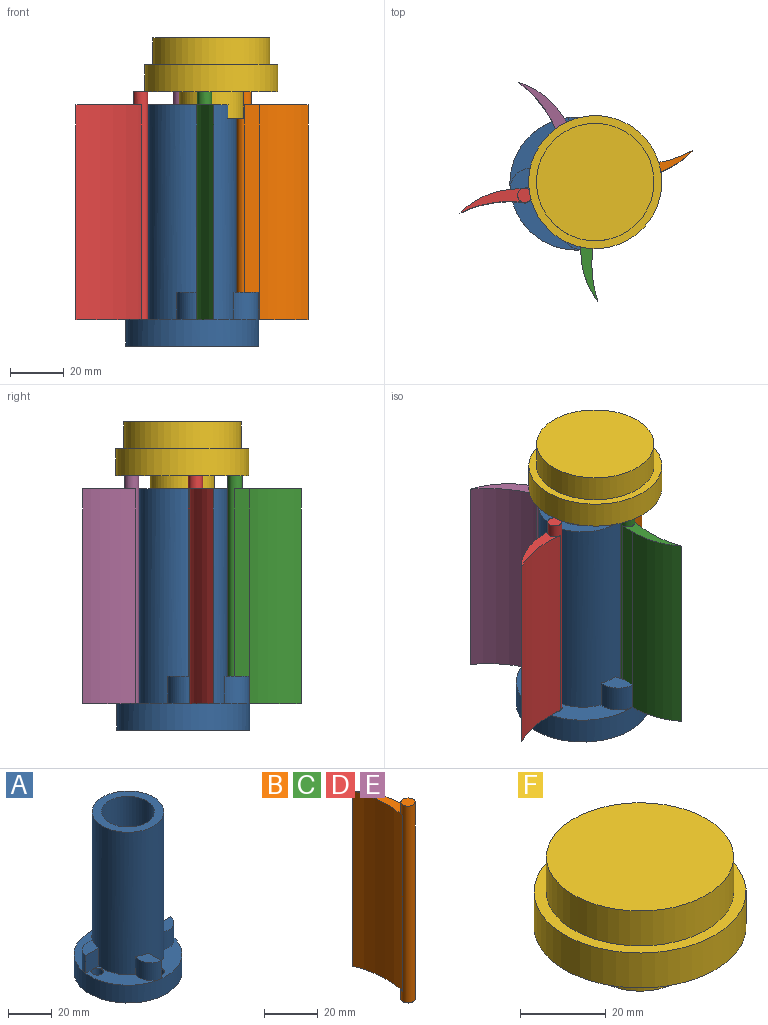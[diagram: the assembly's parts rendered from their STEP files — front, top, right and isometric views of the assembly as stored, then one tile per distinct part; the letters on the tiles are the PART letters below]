
ASSEMBLY  parts=6 mates=5
PART A: 29 faces, bbox 49.6x49.6x90 mm
  f0: plane 27.4x22.05mm, normal (0,0,1), area 194.7mm2, adj f2,f6,f15,f17,f26
  f1: plane 27.4x22.05mm, normal (0,0,1), area 194.7mm2, adj f2,f6,f11,f23,f27
  f2: cylinder r=16.44mm len=80mm, axis (0,0,-1), area 7991mm2, adj f0,f1,f3,f4,f16,f17,f18,f19
  f3: plane 27.4x22.05mm, normal (0,0,1), area 194.7mm2, adj f2,f6,f13,f20,f24
  f4: plane 27.4x22.05mm, normal (0,0,1), area 194.7mm2, adj f2,f6,f9,f18,f21
  f5: cylinder r=12.15mm len=90mm, axis (0,0,-1), area 6870.7mm2, adj f7,f16
  f6: cylinder r=24.8mm len=49.6mm, axis (0,0,-1), area 1558.2mm2, adj f0,f1,f3,f4,f7
  f7: plane 49.6x49.6mm, normal (0,0,-1), area 1468.4mm2, adj f5,f6
  f8: cone r=0mm half-angle=59deg, axis (0,0,1), area 27.7mm2, adj f9
  f9: cylinder r=2.75mm len=5.5mm, axis (0,0,1), area 86.4mm2, adj f4,f8
  f10: cone r=0mm half-angle=59deg, axis (0,0,1), area 27.7mm2, adj f11
  f11: cylinder r=2.75mm len=5.5mm, axis (0,0,1), area 86.4mm2, adj f1,f10
  f12: cone r=0mm half-angle=59deg, axis (0,0,1), area 27.7mm2, adj f13
  f13: cylinder r=2.75mm len=5.5mm, axis (0,0,1), area 86.4mm2, adj f3,f12
  f14: cone r=0mm half-angle=59deg, axis (0,0,1), area 27.7mm2, adj f15
  f15: cylinder r=2.75mm len=5.5mm, axis (0,0,1), area 86.4mm2, adj f0,f14
  f16: plane 32.88x32.88mm, normal (0,0,1), area 385.2mm2, adj f2,f5
  f17: cylinder r=7.92mm len=10.92mm, axis (0,0,-1), area 145.6mm2, adj f0,f2,f18,f19
  f18: plane 10x8.44mm, normal (1,0,0), area 84.4mm2, adj f2,f4,f17,f19
  f19: plane 10.92x6.9mm, normal (0,0,1), area 52.4mm2, adj f2,f17,f18
  f20: plane 10x8.44mm, normal (0,1,0), area 84.4mm2, adj f2,f3,f21,f22
  f21: cylinder r=7.92mm len=10.92mm, axis (0,0,-1), area 145.6mm2, adj f2,f4,f20,f22
  f22: plane 10.92x6.9mm, normal (0,0,1), area 52.4mm2, adj f2,f20,f21
  f23: plane 10x8.44mm, normal (-1,0,0), area 84.4mm2, adj f1,f2,f24,f25
  f24: cylinder r=7.92mm len=10.92mm, axis (0,0,-1), area 145.6mm2, adj f2,f3,f23,f25
  f25: plane 10.92x6.9mm, normal (0,0,1), area 52.4mm2, adj f2,f23,f24
  f26: plane 10x8.44mm, normal (0,-1,0), area 84.4mm2, adj f0,f2,f27,f28
  f27: cylinder r=7.92mm len=10.92mm, axis (0,0,-1), area 145.6mm2, adj f1,f2,f26,f28
  f28: plane 10.92x6.9mm, normal (0,0,1), area 52.4mm2, adj f2,f26,f27
PART B: 10 faces, bbox 7.1x27.2x89.9 mm
  f0: plane 1.09x0.23mm, normal (0,0,1), area 0mm2, adj f1,f4
  f1: cylinder r=2.65mm len=89.9mm, axis (0,0,-1), area 830.9mm2, adj f0,f2,f3,f4,f5,f7,f8,f9
  f2: plane 5.3x5.3mm, normal (0,0,-1), area 22.1mm2, adj f1
  f3: plane 24.6x7.11mm, normal (0,0,-1), area 67.8mm2, adj f1,f4,f5,f6
  f4: cylinder r=42mm len=80mm, axis (0,0,-1), area 2002.7mm2, adj f0,f1,f3,f6,f7,f9
  f5: plane 80x5.3mm, normal (1,0,0), area 424mm2, adj f1,f3,f6,f7
  f6: cylinder r=29.73mm len=80mm, axis (0,0,-1), area 1680.1mm2, adj f3,f4,f5,f7
  f7: plane 24.6x7.11mm, normal (0,0,1), area 67.8mm2, adj f1,f4,f5,f6
  f8: plane 5.3x5.3mm, normal (0,0,1), area 22.1mm2, adj f1
  f9: plane 1.09x0.23mm, normal (0,0,-1), area 0mm2, adj f1,f4
PART C: same geometry as B
PART D: same geometry as B
PART E: same geometry as B
PART F: 15 faces, bbox 49.6x49.6x30 mm
  f0: cylinder r=24.8mm len=49.6mm, axis (0,0,1), area 1558.2mm2, adj f1,f2
  f1: plane 49.6x49.6mm, normal (0,0,-1), area 1388.5mm2, adj f0,f5,f8,f10,f12,f14
  f2: plane 49.6x49.6mm, normal (0,0,1), area 425.5mm2, adj f0,f3
  f3: cylinder r=21.9mm len=43.8mm, axis (0,0,-1), area 1376mm2, adj f2,f4
  f4: plane 43.8x43.8mm, normal (0,0,1), area 1506.7mm2, adj f3
  f5: cylinder r=11.95mm len=23.9mm, axis (0,0,1), area 750.8mm2, adj f1,f6
  f6: plane 23.9x23.9mm, normal (0,0,-1), area 448.6mm2, adj f5
  f7: cone r=0mm half-angle=59deg, axis (0,0,-1), area 27.7mm2, adj f8
  f8: cylinder r=2.75mm len=5.5mm, axis (0,0,-1), area 86.4mm2, adj f1,f7
  f9: cone r=0mm half-angle=59deg, axis (0,0,-1), area 27.7mm2, adj f10
  f10: cylinder r=2.75mm len=5.5mm, axis (0,0,-1), area 86.4mm2, adj f1,f9
  f11: cone r=0mm half-angle=59deg, axis (0,0,-1), area 27.7mm2, adj f12
  f12: cylinder r=2.75mm len=5.5mm, axis (0,0,-1), area 86.4mm2, adj f1,f11
  f13: cone r=0mm half-angle=59deg, axis (0,0,-1), area 27.7mm2, adj f14
  f14: cylinder r=2.75mm len=5.5mm, axis (0,0,-1), area 86.4mm2, adj f1,f13
PLACE A rot(axis=(0,0,1),13.2deg) t=(-0.23,15.57,25.57)mm fixed
PLACE B rot(axis=(0,0,-1),82.7deg) t=(19.05,20.1,30.57)mm
PLACE C rot(axis=(0,0,1),177.8deg) t=(4.3,-3.71,30.57)mm
PLACE D rot(axis=(0,0,1),95deg) t=(-19.5,11.04,30.57)mm
PLACE E rot(axis=(0,0,1),32.6deg) t=(-4.76,34.84,30.57)mm
PLACE F rot(axis=(0,0,-1),7.2deg) t=(6.78,15.94,130.47)mm
MATE revolute B.f1 <-> A.f12  axis (0,0,-1) through (19.05,20.1,30.57)mm
MATE revolute D.f1 <-> A.f14  axis (0,0,-1) through (-19.5,11.04,30.57)mm
MATE revolute C.f1 <-> A.f8  axis (0,0,-1) through (4.3,-3.71,30.57)mm
MATE revolute C.f1 <-> F.f11  axis (0,0,1) through (4.3,-3.71,120.47)mm
MATE revolute E.f1 <-> A.f10  axis (0,0,-1) through (-4.76,34.84,30.57)mm
